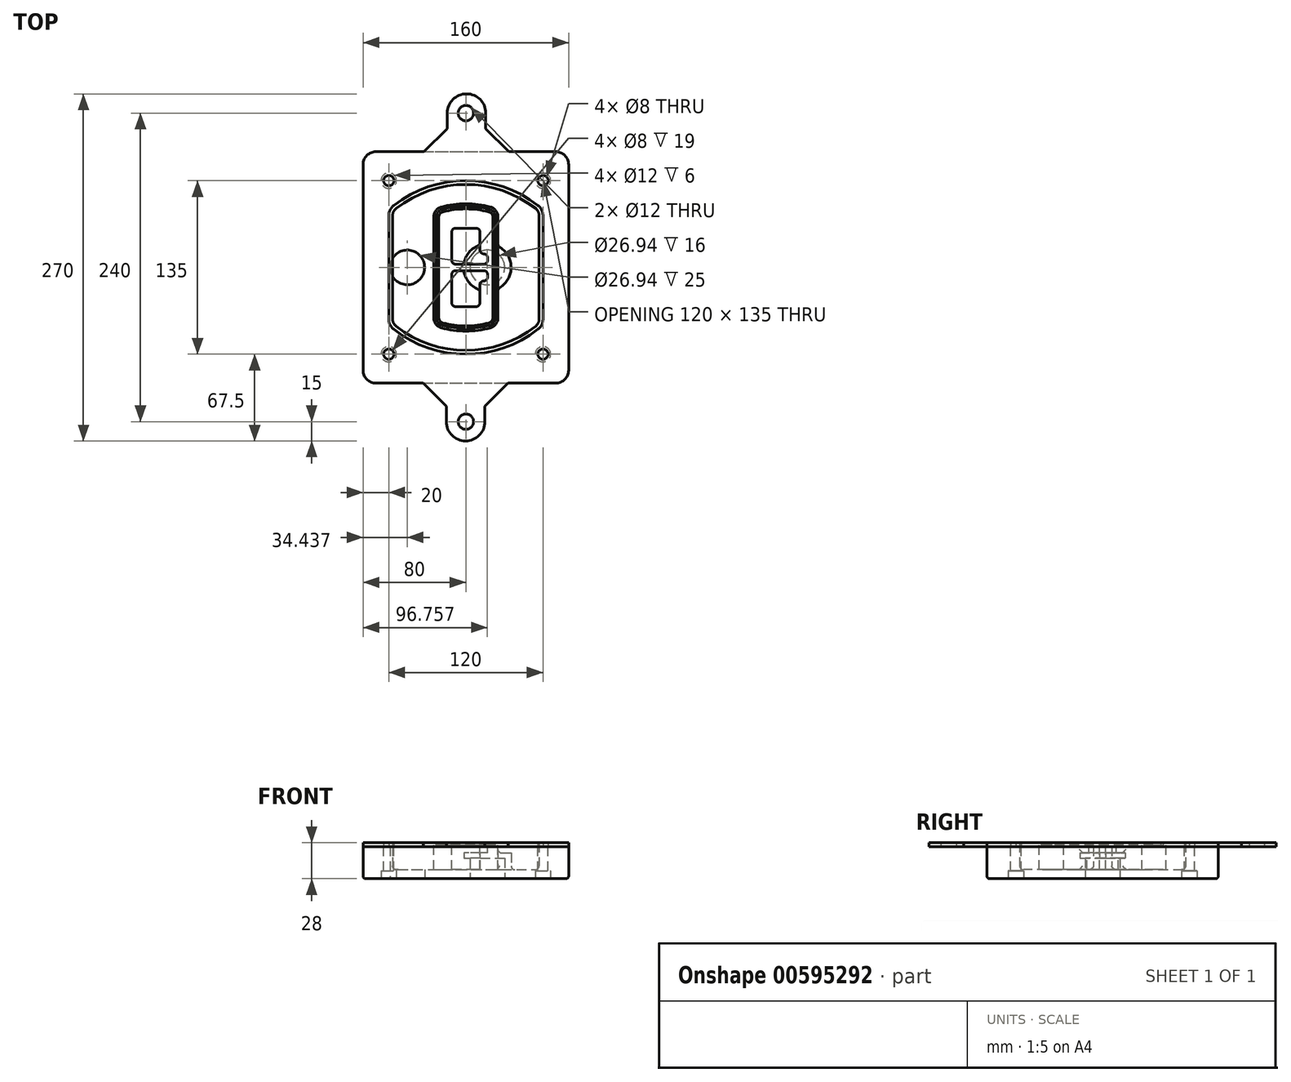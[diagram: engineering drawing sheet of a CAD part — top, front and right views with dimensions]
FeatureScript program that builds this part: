
annotation { "Feature Type Name" : "Feature", "Feature Type Description" : "" }
export const myFeature = defineFeature(function(context is Context, id is Id, definition is map)
    precondition{}
    {
        {
            var Q0;
            Q0=qCreatedBy(makeId("Top.planeOp"),FACE);
            var sketch = newSketch(context, id + "F0", { "sketchPlane" : qUnion([Q0])});
            skPoint(sketch, "E0.rect.middle", {"position": v(0, 0) * mm});
            skLineSegment(sketch, "E1.bottom", {"start": v(-70, -90) * mm, "end": v(70, -90) * mm});
            skLineSegment(sketch, "E1.top", {"start": v(-70, 90) * mm, "end": v(70, 90) * mm});
            skLineSegment(sketch, "E1.left", {"start": v(-80, -80) * mm, "end": v(-80, 80) * mm});
            skLineSegment(sketch, "E1.right", {"start": v(80, -80) * mm, "end": v(80, 80) * mm});
            skLineSegment(sketch, "E2", {"start": v(-80, 90) * mm, "end": v(80, -90) * mm, "construction": true});
            skLineSegment(sketch, "E3", {"start": v(80, 90) * mm, "end": v(-80, -90) * mm, "construction": true});
            skCircle(sketch, "E4", {"center": v(-60, 67.5) * mm, "radius": 4 * mm});
            skCircle(sketch, "E5", {"center": v(60, 67.5) * mm, "radius": 4 * mm});
            skCircle(sketch, "E6", {"center": v(60, -67.5) * mm, "radius": 4 * mm});
            skCircle(sketch, "E7", {"center": v(-60, -67.5) * mm, "radius": 4 * mm});
            skLineSegment(sketch, "E8", {"start": v(-60, 67.5) * mm, "end": v(60, 67.5) * mm, "construction": true});
            skLineSegment(sketch, "E9", {"start": v(60, 67.5) * mm, "end": v(60, -67.5) * mm, "construction": true});
            skLineSegment(sketch, "E10", {"start": v(60, -67.5) * mm, "end": v(-60, -67.5) * mm, "construction": true});
            skLineSegment(sketch, "E11", {"start": v(-60, -67.5) * mm, "end": v(-60, 67.5) * mm, "construction": true});
            skLineSegment(sketch, "E12", {"start": v(-60, 40.3) * mm, "end": v(-60, -40.3) * mm});
            skLineSegment(sketch, "E13", {"start": v(60, 40.3) * mm, "end": v(60, -40.3) * mm});
            skArc(sketch, "E14", {"start": v(56.15, 48.18) * mm, "mid": v(0, 67.5) * mm, "end": v(-56.15, 48.18) * mm});
            skArc(sketch, "E15", {"start": v(-56.15, -48.18) * mm, "mid": v(0, -67.5) * mm, "end": v(56.15, -48.18) * mm});
            skLineSegment(sketch, "E16", {"start": v(-60, 0) * mm, "end": v(60, 0) * mm, "construction": true});
            skPoint(sketch, "E17.visualSharp", {"position": v(-60, -45) * mm});
            skArc(sketch, "E17.filletArc", {"start": v(-60, -40.3) * mm, "mid": v(-58.99, -44.68) * mm, "end": v(-56.15, -48.18) * mm});
            skPoint(sketch, "E18.visualSharp", {"position": v(-60, 45) * mm});
            skArc(sketch, "E18.filletArc", {"start": v(-56.15, 48.18) * mm, "mid": v(-58.99, 44.68) * mm, "end": v(-60, 40.3) * mm});
            skPoint(sketch, "E19.visualSharp", {"position": v(60, 45) * mm});
            skArc(sketch, "E19.filletArc", {"start": v(60, 40.3) * mm, "mid": v(58.99, 44.68) * mm, "end": v(56.15, 48.18) * mm});
            skPoint(sketch, "E20.visualSharp", {"position": v(60, -45) * mm});
            skArc(sketch, "E20.filletArc", {"start": v(56.15, -48.18) * mm, "mid": v(58.99, -44.68) * mm, "end": v(60, -40.3) * mm});
            skPoint(sketch, "E21.visualSharp", {"position": v(-80, 90) * mm});
            skArc(sketch, "E21.filletArc", {"start": v(-70, 90) * mm, "mid": v(-77.07, 87.07) * mm, "end": v(-80, 80) * mm});
            skPoint(sketch, "E22.visualSharp", {"position": v(80, 90) * mm});
            skArc(sketch, "E22.filletArc", {"start": v(80, 80) * mm, "mid": v(77.07, 87.07) * mm, "end": v(70, 90) * mm});
            skPoint(sketch, "E23.visualSharp", {"position": v(80, -90) * mm});
            skArc(sketch, "E23.filletArc", {"start": v(70, -90) * mm, "mid": v(77.07, -87.07) * mm, "end": v(80, -80) * mm});
            skPoint(sketch, "E24.visualSharp", {"position": v(-80, -90) * mm});
            skArc(sketch, "E24.filletArc", {"start": v(-80, -80) * mm, "mid": v(-77.07, -87.07) * mm, "end": v(-70, -90) * mm});
            skArc(sketch, "E25.0", {"start": v(57, 40.3) * mm, "mid": v(56.3, 43.36) * mm, "end": v(54.3, 45.81) * mm});
            skLineSegment(sketch, "E25.1", {"start": v(57, 40.3) * mm, "end": v(57, -40.3) * mm});
            skArc(sketch, "E25.2", {"start": v(54.3, -45.81) * mm, "mid": v(56.3, -43.36) * mm, "end": v(57, -40.3) * mm});
            skArc(sketch, "E25.3", {"start": v(-54.3, -45.81) * mm, "mid": v(0, -64.5) * mm, "end": v(54.3, -45.81) * mm});
            skArc(sketch, "E25.4", {"start": v(-57, -40.3) * mm, "mid": v(-56.3, -43.36) * mm, "end": v(-54.3, -45.81) * mm});
            skArc(sketch, "E25.5", {"start": v(54.3, 45.81) * mm, "mid": v(0, 64.5) * mm, "end": v(-54.3, 45.81) * mm});
            skLineSegment(sketch, "E25.6", {"start": v(-57, 40.3) * mm, "end": v(-57, -40.3) * mm});
            skArc(sketch, "E25.7", {"start": v(-54.3, 45.81) * mm, "mid": v(-56.3, 43.36) * mm, "end": v(-57, 40.3) * mm});
            skArc(sketch, "E26.0", {"start": v(-58.62, 51.33) * mm, "mid": v(-62.58, 46.43) * mm, "end": v(-64, 40.3) * mm});
            skArc(sketch, "E26.1", {"start": v(58.62, 51.33) * mm, "mid": v(0, 71.5) * mm, "end": v(-58.62, 51.33) * mm});
            skArc(sketch, "E26.2", {"start": v(64, 40.3) * mm, "mid": v(62.58, 46.43) * mm, "end": v(58.62, 51.33) * mm});
            skLineSegment(sketch, "E26.3", {"start": v(64, 40.3) * mm, "end": v(64, -40.3) * mm});
            skArc(sketch, "E26.4", {"start": v(58.62, -51.33) * mm, "mid": v(62.58, -46.43) * mm, "end": v(64, -40.3) * mm});
            skLineSegment(sketch, "E26.5", {"start": v(-64, 40.3) * mm, "end": v(-64, -40.3) * mm});
            skArc(sketch, "E26.6", {"start": v(-58.62, -51.33) * mm, "mid": v(0, -71.5) * mm, "end": v(58.62, -51.33) * mm});
            skArc(sketch, "E26.7", {"start": v(-64, -40.3) * mm, "mid": v(-62.58, -46.43) * mm, "end": v(-58.62, -51.33) * mm});
            skSolve(sketch);
        }
        {
            var Q0;
            Q0=makeQuery(id+"F0.imprint","IMPRINT",FACE,{"disambiguationData":[TD([[makeQuery(id+"F0.imprint","IMPRINT",EDGE,{"derivedFrom":sQuery(id+"F0.wireOp",EDGE,"E1.bottom")}),1.0]])]});
            var Q1;
            Q1=makeQuery(id+"F0.imprint","IMPRINT",FACE,{"disambiguationData":[TD([[makeQuery(id+"F0.imprint","IMPRINT",EDGE,{"derivedFrom":sQuery(id+"F0.wireOp",EDGE,"E12")}),1.0]])]});
            var Q2;
            Q2=makeQuery(id+"F0.imprint","IMPRINT",FACE,{"disambiguationData":[TD([[makeQuery(id+"F0.imprint","IMPRINT",EDGE,{"derivedFrom":sQuery(id+"F0.wireOp",EDGE,"E25.0")}),1.0]])]});
            var Q3;
            Q3=makeQuery(id+"F0.imprint","IMPRINT",FACE,{"disambiguationData":[TD([[makeQuery(id+"F0.imprint","IMPRINT",EDGE,{"derivedFrom":sQuery(id+"F0.wireOp",EDGE,"E12")}),-1.0]])]});
            extrude(context, id + "F1", {"entities" : qUnion([Q0, Q1, Q2, Q3]), "oppositeDirection" : true, "depth" : 25 * mm});
        }
        {
            var Q0;
            Q0=makeQuery(id+"F0.imprint","IMPRINT",FACE,{"disambiguationData":[TD([[makeQuery(id+"F0.imprint","IMPRINT",EDGE,{"derivedFrom":sQuery(id+"F0.wireOp",EDGE,"E12")}),1.0]])]});
            extrude(context, id + "F2", {"entities" : qUnion([Q0]), "operationType" : NewBodyOperationType.ADD, "depth" : 3 * mm});
        }
        {
            var Q0;
            Q0=makeQuery(id+"F0.imprint","IMPRINT",FACE,{"disambiguationData":[TD([[makeQuery(id+"F0.imprint","IMPRINT",EDGE,{"derivedFrom":sQuery(id+"F0.wireOp",EDGE,"E25.0")}),1.0]])]});
            extrude(context, id + "F3", {"entities" : qUnion([Q0]), "operationType" : NewBodyOperationType.REMOVE, "oppositeDirection" : true, "depth" : 18 * mm});
        }
        {
            var Q0;
            Q0=makeQuery(id+"F2.opExtrude","CAP_FACE",FACE,{"disambiguationData":[OSD([sQuery(id+"F0.wireOp",EDGE,"E12"),sQuery(id+"F0.wireOp",EDGE,"E13"),sQuery(id+"F0.wireOp",EDGE,"E14"),sQuery(id+"F0.wireOp",EDGE,"E15"),sQuery(id+"F0.wireOp",EDGE,"E17.filletArc"),sQuery(id+"F0.wireOp",EDGE,"E18.filletArc"),sQuery(id+"F0.wireOp",EDGE,"E19.filletArc"),sQuery(id+"F0.wireOp",EDGE,"E20.filletArc"),sQuery(id+"F0.wireOp",EDGE,"E25.0"),sQuery(id+"F0.wireOp",EDGE,"E25.1"),sQuery(id+"F0.wireOp",EDGE,"E25.2"),sQuery(id+"F0.wireOp",EDGE,"E25.3"),sQuery(id+"F0.wireOp",EDGE,"E25.4"),sQuery(id+"F0.wireOp",EDGE,"E25.5"),sQuery(id+"F0.wireOp",EDGE,"E25.6"),sQuery(id+"F0.wireOp",EDGE,"E25.7")])],"isStart":false});
            var sketch = newSketch(context, id + "F4", { "sketchPlane" : qUnion([Q0])});
            skArc(sketch, "E27.0", {"start": v(-19.08, -46.97) * mm, "mid": v(0, -49.5) * mm, "end": v(19.08, -46.97) * mm});
            skArc(sketch, "E28.0", {"start": v(19.08, 46.97) * mm, "mid": v(0, 49.5) * mm, "end": v(-19.08, 46.97) * mm});
            skLineSegment(sketch, "E29", {"start": v(-25, 39.25) * mm, "end": v(-25, -39.25) * mm});
            skLineSegment(sketch, "E30", {"start": v(25, 39.25) * mm, "end": v(25, -39.25) * mm});
            skLineSegment(sketch, "E31", {"start": v(-25, 45.1) * mm, "end": v(25, 45.1) * mm, "construction": true});
            skLineSegment(sketch, "E32", {"start": v(-25, -45.1) * mm, "end": v(25, -45.1) * mm, "construction": true});
            skPoint(sketch, "E33.visualSharp", {"position": v(-25, 45.1) * mm});
            skArc(sketch, "E33.filletArc", {"start": v(-19.08, 46.97) * mm, "mid": v(-23.35, 44.11) * mm, "end": v(-25, 39.25) * mm});
            skPoint(sketch, "E34.visualSharp", {"position": v(25, 45.1) * mm});
            skArc(sketch, "E34.filletArc", {"start": v(25, 39.25) * mm, "mid": v(23.35, 44.11) * mm, "end": v(19.08, 46.97) * mm});
            skPoint(sketch, "E35.visualSharp", {"position": v(25, -45.1) * mm});
            skArc(sketch, "E35.filletArc", {"start": v(19.08, -46.97) * mm, "mid": v(23.35, -44.11) * mm, "end": v(25, -39.25) * mm});
            skPoint(sketch, "E36.visualSharp", {"position": v(-25, -45.1) * mm});
            skArc(sketch, "E36.filletArc", {"start": v(-25, -39.25) * mm, "mid": v(-23.35, -44.11) * mm, "end": v(-19.08, -46.97) * mm});
            skArc(sketch, "E37.0", {"start": v(54.3, 45.81) * mm, "mid": v(0, 64.5) * mm, "end": v(-54.3, 45.81) * mm});
            skArc(sketch, "E37.1", {"start": v(-54.3, 45.81) * mm, "mid": v(-56.3, 43.36) * mm, "end": v(-57, 40.3) * mm});
            skLineSegment(sketch, "E37.2", {"start": v(-57, 40.3) * mm, "end": v(-57, -40.3) * mm});
            skArc(sketch, "E37.3", {"start": v(-57, -40.3) * mm, "mid": v(-56.3, -43.36) * mm, "end": v(-54.3, -45.81) * mm});
            skArc(sketch, "E37.4", {"start": v(-54.3, -45.81) * mm, "mid": v(0, -64.5) * mm, "end": v(54.3, -45.81) * mm});
            skArc(sketch, "E37.5", {"start": v(54.3, -45.81) * mm, "mid": v(56.3, -43.36) * mm, "end": v(57, -40.3) * mm});
            skLineSegment(sketch, "E37.6", {"start": v(57, 40.3) * mm, "end": v(57, -40.3) * mm});
            skArc(sketch, "E37.7", {"start": v(57, 40.3) * mm, "mid": v(56.3, 43.36) * mm, "end": v(54.3, 45.81) * mm});
            skLineSegment(sketch, "E38.0", {"start": v(23, 39.25) * mm, "end": v(23, -39.25) * mm});
            skArc(sketch, "E38.1", {"start": v(18.56, -45.04) * mm, "mid": v(21.76, -42.9) * mm, "end": v(23, -39.25) * mm});
            skArc(sketch, "E38.2", {"start": v(-18.56, -45.04) * mm, "mid": v(0, -47.5) * mm, "end": v(18.56, -45.04) * mm});
            skArc(sketch, "E38.3", {"start": v(-23, -39.25) * mm, "mid": v(-21.76, -42.9) * mm, "end": v(-18.56, -45.04) * mm});
            skLineSegment(sketch, "E38.4", {"start": v(-23, 39.25) * mm, "end": v(-23, -39.25) * mm});
            skArc(sketch, "E38.5", {"start": v(23, 39.25) * mm, "mid": v(21.76, 42.9) * mm, "end": v(18.56, 45.04) * mm});
            skArc(sketch, "E38.6", {"start": v(-18.56, 45.04) * mm, "mid": v(-21.76, 42.9) * mm, "end": v(-23, 39.25) * mm});
            skArc(sketch, "E38.7", {"start": v(18.56, 45.04) * mm, "mid": v(0, 47.5) * mm, "end": v(-18.56, 45.04) * mm});
            skArc(sketch, "E39.0", {"start": v(21, 39.25) * mm, "mid": v(20.18, 41.68) * mm, "end": v(18.04, 43.1) * mm});
            skLineSegment(sketch, "E39.1", {"start": v(21, 39.25) * mm, "end": v(21, -39.25) * mm});
            skArc(sketch, "E39.2", {"start": v(18.04, -43.1) * mm, "mid": v(20.18, -41.68) * mm, "end": v(21, -39.25) * mm});
            skArc(sketch, "E39.3", {"start": v(-18.04, -43.1) * mm, "mid": v(0, -45.5) * mm, "end": v(18.04, -43.1) * mm});
            skArc(sketch, "E39.4", {"start": v(-21, -39.25) * mm, "mid": v(-20.18, -41.68) * mm, "end": v(-18.04, -43.1) * mm});
            skArc(sketch, "E39.5", {"start": v(18.04, 43.1) * mm, "mid": v(0, 45.5) * mm, "end": v(-18.04, 43.1) * mm});
            skLineSegment(sketch, "E39.6", {"start": v(-21, 39.25) * mm, "end": v(-21, -39.25) * mm});
            skArc(sketch, "E39.7", {"start": v(-18.04, 43.1) * mm, "mid": v(-20.18, 41.68) * mm, "end": v(-21, 39.25) * mm});
            skLineSegment(sketch, "E40", {"start": v(-25, 0) * mm, "end": v(25, 0) * mm, "construction": true});
            skLineSegment(sketch, "E41", {"start": v(-11, 5.5) * mm, "end": v(-11, 27.5) * mm});
            skLineSegment(sketch, "E42", {"start": v(-8, 30.5) * mm, "end": v(8, 30.5) * mm});
            skLineSegment(sketch, "E43", {"start": v(11, 27.5) * mm, "end": v(11, 13.5) * mm});
            skLineSegment(sketch, "E44", {"start": v(14, 10.5) * mm, "end": v(14, 10.5) * mm});
            skLineSegment(sketch, "E45", {"start": v(17, 7.5) * mm, "end": v(17, 5.5) * mm});
            skLineSegment(sketch, "E46", {"start": v(14, 2.5) * mm, "end": v(-8, 2.5) * mm});
            skPoint(sketch, "E47.visualSharp", {"position": v(-11, 30.5) * mm});
            skArc(sketch, "E47.filletArc", {"start": v(-8, 30.5) * mm, "mid": v(-10.12, 29.62) * mm, "end": v(-11, 27.5) * mm});
            skPoint(sketch, "E48.visualSharp", {"position": v(11, 30.5) * mm});
            skArc(sketch, "E48.filletArc", {"start": v(11, 27.5) * mm, "mid": v(10.12, 29.62) * mm, "end": v(8, 30.5) * mm});
            skPoint(sketch, "E49.visualSharp", {"position": v(11, 10.5) * mm});
            skArc(sketch, "E49.filletArc", {"start": v(11, 13.5) * mm, "mid": v(11.88, 11.38) * mm, "end": v(14, 10.5) * mm});
            skPoint(sketch, "E50.visualSharp", {"position": v(17, 10.5) * mm});
            skArc(sketch, "E50.filletArc", {"start": v(17, 7.5) * mm, "mid": v(16.12, 9.62) * mm, "end": v(14, 10.5) * mm});
            skPoint(sketch, "E51.visualSharp", {"position": v(17, 2.5) * mm});
            skArc(sketch, "E51.filletArc", {"start": v(14, 2.5) * mm, "mid": v(16.12, 3.38) * mm, "end": v(17, 5.5) * mm});
            skPoint(sketch, "E52.visualSharp", {"position": v(-11, 2.5) * mm});
            skArc(sketch, "E52.filletArc", {"start": v(-11, 5.5) * mm, "mid": v(-10.12, 3.38) * mm, "end": v(-8, 2.5) * mm});
            skLineSegment(sketch, "E53.0.MirrorCS", {"start": v(14, -2.5) * mm, "end": v(-8, -2.5) * mm});
            skArc(sketch, "E54.0.MirrorCS", {"start": v(-11, -5.5) * mm, "mid": v(-10.12, -3.38) * mm, "end": v(-8, -2.5) * mm});
            skLineSegment(sketch, "E55.0.MirrorCS", {"start": v(-11, -5.5) * mm, "end": v(-11, -27.5) * mm});
            skArc(sketch, "E56.0.MirrorCS", {"start": v(-8, -30.5) * mm, "mid": v(-10.12, -29.62) * mm, "end": v(-11, -27.5) * mm});
            skLineSegment(sketch, "E57.0.MirrorCS", {"start": v(-8, -30.5) * mm, "end": v(8, -30.5) * mm});
            skArc(sketch, "E58.0.MirrorCS", {"start": v(11, -27.5) * mm, "mid": v(10.12, -29.62) * mm, "end": v(8, -30.5) * mm});
            skLineSegment(sketch, "E59.0.MirrorCS", {"start": v(11, -27.5) * mm, "end": v(11, -13.5) * mm});
            skArc(sketch, "E60.0.MirrorCS", {"start": v(11, -13.5) * mm, "mid": v(11.88, -11.38) * mm, "end": v(14, -10.5) * mm});
            skArc(sketch, "E61.0.MirrorCS", {"start": v(17, -7.5) * mm, "mid": v(16.12, -9.62) * mm, "end": v(14, -10.5) * mm});
            skLineSegment(sketch, "E62.0.MirrorCS", {"start": v(17, -7.5) * mm, "end": v(17, -5.5) * mm});
            skArc(sketch, "E63.0.MirrorCS", {"start": v(14, -2.5) * mm, "mid": v(16.12, -3.38) * mm, "end": v(17, -5.5) * mm});
            skSolve(sketch);
        }
        {
            var Q0;
            Q0=makeQuery(id+"F4.imprint","IMPRINT",FACE,{"disambiguationData":[TD([[makeQuery(id+"F4.imprint","IMPRINT",EDGE,{"derivedFrom":sQuery(id+"F4.wireOp",EDGE,"E27.0")}),1.0]])]});
            var Q1;
            Q1=makeQuery(id+"F4.imprint","IMPRINT",FACE,{"disambiguationData":[TD([[makeQuery(id+"F4.imprint","IMPRINT",EDGE,{"derivedFrom":sQuery(id+"F4.wireOp",EDGE,"E38.0")}),-1.0]])]});
            var Q2;
            Q2=makeQuery(id+"F4.imprint","IMPRINT",FACE,{"disambiguationData":[TD([[makeQuery(id+"F4.imprint","IMPRINT",EDGE,{"derivedFrom":sQuery(id+"F4.wireOp",EDGE,"E39.0")}),1.0]])]});
            extrude(context, id + "F5", {"entities" : qUnion([Q0, Q1, Q2]), "operationType" : NewBodyOperationType.ADD, "endBound" : BoundingType.UP_TO_NEXT, "oppositeDirection" : true, "depth" : 25 * mm});
        }
        {
            var Q0;
            Q0=makeQuery(id+"F4.imprint","IMPRINT",FACE,{"disambiguationData":[TD([[makeQuery(id+"F4.imprint","IMPRINT",EDGE,{"derivedFrom":sQuery(id+"F4.wireOp",EDGE,"E38.0")}),-1.0]])]});
            extrude(context, id + "F6", {"entities" : qUnion([Q0]), "operationType" : NewBodyOperationType.REMOVE, "oppositeDirection" : true, "depth" : 2 * mm});
        }
        {
            var Q0;
            Q0=makeQuery(id+"F1.opExtrude","CAP_FACE",FACE,{"disambiguationData":[OSD([sQuery(id+"F0.wireOp",EDGE,"E1.bottom"),sQuery(id+"F0.wireOp",EDGE,"E1.top"),sQuery(id+"F0.wireOp",EDGE,"E1.left"),sQuery(id+"F0.wireOp",EDGE,"E1.right"),sQuery(id+"F0.wireOp",EDGE,"E4"),sQuery(id+"F0.wireOp",EDGE,"E5"),sQuery(id+"F0.wireOp",EDGE,"E6"),sQuery(id+"F0.wireOp",EDGE,"E7"),sQuery(id+"F0.wireOp",EDGE,"E21.filletArc"),sQuery(id+"F0.wireOp",EDGE,"E22.filletArc"),sQuery(id+"F0.wireOp",EDGE,"E23.filletArc"),sQuery(id+"F0.wireOp",EDGE,"E24.filletArc")])],"isStart":false});
            var sketch = newSketch(context, id + "F7", { "sketchPlane" : qUnion([Q0])});
            skCircle(sketch, "E64", {"center": v(16.76, 0) * mm, "radius": 13.47 * mm});
            skCircle(sketch, "E65", {"center": v(-45.56, 0) * mm, "radius": 13.47 * mm});
            skLineSegment(sketch, "E66", {"start": v(80, 0) * mm, "end": v(-80, 0) * mm});
            skCircle(sketch, "E67", {"center": v(16.76, 0) * mm, "radius": 18.47 * mm});
            skCircle(sketch, "E68", {"center": v(60, -67.5) * mm, "radius": 6 * mm});
            skCircle(sketch, "E69", {"center": v(-60, -67.5) * mm, "radius": 6 * mm});
            skCircle(sketch, "E70", {"center": v(-60, 67.5) * mm, "radius": 6 * mm});
            skCircle(sketch, "E71", {"center": v(60, 67.5) * mm, "radius": 6 * mm});
            skSolve(sketch);
        }
        {
            var Q0;
            {var subQ1=sQuery(id+"F7.wireOp",EDGE,"E66");var subQ4=sQuery(id+"F7.wireOp",EDGE,"E64");var subQ6=makeQuery(id+"F7.imprint","INTERSECT",VERTEX,{"disambiguationData":[OD(0.0)],"derivedFrom":[subQ4,subQ1]});Q0=makeQuery(id+"F7.imprint","IMPRINT",FACE,{"disambiguationData":[TD([[makeQuery(id+"F7.imprint","IMPRINT",EDGE,{"disambiguationData":[TD([[subQ6,-1.0]])],"derivedFrom":subQ4}),-1.0]])]});}
            var Q1;
            {var subQ0=sQuery(id+"F7.wireOp",EDGE,"E66");var subQ1=sQuery(id+"F7.wireOp",EDGE,"E64");var subQ3=makeQuery(id+"F7.imprint","INTERSECT",VERTEX,{"disambiguationData":[OD(0.0)],"derivedFrom":[subQ1,subQ0]});Q1=makeQuery(id+"F7.imprint","IMPRINT",FACE,{"disambiguationData":[TD([[makeQuery(id+"F7.imprint","IMPRINT",EDGE,{"disambiguationData":[TD([[subQ3,-1.0]])],"derivedFrom":subQ1}),1.0]])]});}
            var Q2;
            {var subQ0=sQuery(id+"F7.wireOp",EDGE,"E66");var subQ1=sQuery(id+"F7.wireOp",EDGE,"E64");var subQ3=makeQuery(id+"F7.imprint","INTERSECT",VERTEX,{"disambiguationData":[OD(0.0)],"derivedFrom":[subQ1,subQ0]});Q2=makeQuery(id+"F7.imprint","IMPRINT",FACE,{"disambiguationData":[TD([[makeQuery(id+"F7.imprint","IMPRINT",EDGE,{"disambiguationData":[TD([[subQ3,1.0]])],"derivedFrom":subQ1}),1.0]])]});}
            var Q3;
            {var subQ1=sQuery(id+"F7.wireOp",EDGE,"E66");var subQ4=sQuery(id+"F7.wireOp",EDGE,"E64");var subQ6=makeQuery(id+"F7.imprint","INTERSECT",VERTEX,{"disambiguationData":[OD(0.0)],"derivedFrom":[subQ4,subQ1]});Q3=makeQuery(id+"F7.imprint","IMPRINT",FACE,{"disambiguationData":[TD([[makeQuery(id+"F7.imprint","IMPRINT",EDGE,{"disambiguationData":[TD([[subQ6,1.0]])],"derivedFrom":subQ4}),-1.0]])]});}
            extrude(context, id + "F8", {"entities" : qUnion([Q0, Q1, Q2, Q3]), "operationType" : NewBodyOperationType.ADD, "oppositeDirection" : true, "depth" : 20 * mm});
        }
        {
            var Q0;
            {var subQ0=sQuery(id+"F7.wireOp",EDGE,"E66");var subQ1=sQuery(id+"F7.wireOp",EDGE,"E64");var subQ3=makeQuery(id+"F7.imprint","INTERSECT",VERTEX,{"disambiguationData":[OD(0.0)],"derivedFrom":[subQ1,subQ0]});Q0=makeQuery(id+"F7.imprint","IMPRINT",FACE,{"disambiguationData":[TD([[makeQuery(id+"F7.imprint","IMPRINT",EDGE,{"disambiguationData":[TD([[subQ3,-1.0]])],"derivedFrom":subQ1}),1.0]])]});}
            var Q1;
            {var subQ0=sQuery(id+"F7.wireOp",EDGE,"E66");var subQ1=sQuery(id+"F7.wireOp",EDGE,"E64");var subQ3=makeQuery(id+"F7.imprint","INTERSECT",VERTEX,{"disambiguationData":[OD(0.0)],"derivedFrom":[subQ1,subQ0]});Q1=makeQuery(id+"F7.imprint","IMPRINT",FACE,{"disambiguationData":[TD([[makeQuery(id+"F7.imprint","IMPRINT",EDGE,{"disambiguationData":[TD([[subQ3,1.0]])],"derivedFrom":subQ1}),1.0]])]});}
            extrude(context, id + "F9", {"entities" : qUnion([Q0, Q1]), "operationType" : NewBodyOperationType.REMOVE, "oppositeDirection" : true, "depth" : 16 * mm});
        }
        {
            var Q0;
            {var subQ0=sQuery(id+"F7.wireOp",EDGE,"E66");var subQ1=sQuery(id+"F7.wireOp",EDGE,"E65");var subQ3=makeQuery(id+"F7.imprint","INTERSECT",VERTEX,{"disambiguationData":[OD(0.0)],"derivedFrom":[subQ1,subQ0]});Q0=makeQuery(id+"F7.imprint","IMPRINT",FACE,{"disambiguationData":[TD([[makeQuery(id+"F7.imprint","IMPRINT",EDGE,{"disambiguationData":[TD([[subQ3,-1.0]])],"derivedFrom":subQ1}),1.0]])]});}
            var Q1;
            {var subQ0=sQuery(id+"F7.wireOp",EDGE,"E66");var subQ1=sQuery(id+"F7.wireOp",EDGE,"E65");var subQ3=makeQuery(id+"F7.imprint","INTERSECT",VERTEX,{"disambiguationData":[OD(0.0)],"derivedFrom":[subQ1,subQ0]});Q1=makeQuery(id+"F7.imprint","IMPRINT",FACE,{"disambiguationData":[TD([[makeQuery(id+"F7.imprint","IMPRINT",EDGE,{"disambiguationData":[TD([[subQ3,1.0]])],"derivedFrom":subQ1}),1.0]])]});}
            extrude(context, id + "F10", {"entities" : qUnion([Q0, Q1]), "operationType" : NewBodyOperationType.REMOVE, "oppositeDirection" : true, "depth" : 25 * mm});
        }
        {
            var Q0;
            Q0=makeQuery(id+"F7.imprint","IMPRINT",FACE,{"disambiguationData":[TD([[makeQuery(id+"F7.imprint","IMPRINT",EDGE,{"derivedFrom":sQuery(id+"F7.wireOp",EDGE,"E68")}),1.0]])]});
            var Q1;
            Q1=makeQuery(id+"F7.imprint","IMPRINT",FACE,{"disambiguationData":[TD([[makeQuery(id+"F7.imprint","IMPRINT",EDGE,{"derivedFrom":makeQuery(id+"F1.opExtrude","CAP_EDGE",EDGE,{"disambiguationData":[OSD([sQuery(id+"F0.wireOp",EDGE,"E5")])],"isStart":false})}),-1.0]])]});
            var Q2;
            Q2=makeQuery(id+"F7.imprint","IMPRINT",FACE,{"disambiguationData":[TD([[makeQuery(id+"F7.imprint","IMPRINT",EDGE,{"derivedFrom":sQuery(id+"F7.wireOp",EDGE,"E69")}),1.0]])]});
            var Q3;
            Q3=makeQuery(id+"F7.imprint","IMPRINT",FACE,{"disambiguationData":[TD([[makeQuery(id+"F7.imprint","IMPRINT",EDGE,{"derivedFrom":makeQuery(id+"F1.opExtrude","CAP_EDGE",EDGE,{"disambiguationData":[OSD([sQuery(id+"F0.wireOp",EDGE,"E4")])],"isStart":false})}),-1.0]])]});
            var Q4;
            Q4=makeQuery(id+"F7.imprint","IMPRINT",FACE,{"disambiguationData":[TD([[makeQuery(id+"F7.imprint","IMPRINT",EDGE,{"derivedFrom":sQuery(id+"F7.wireOp",EDGE,"E70")}),1.0]])]});
            var Q5;
            Q5=makeQuery(id+"F7.imprint","IMPRINT",FACE,{"disambiguationData":[TD([[makeQuery(id+"F7.imprint","IMPRINT",EDGE,{"derivedFrom":makeQuery(id+"F1.opExtrude","CAP_EDGE",EDGE,{"disambiguationData":[OSD([sQuery(id+"F0.wireOp",EDGE,"E7")])],"isStart":false})}),-1.0]])]});
            var Q6;
            Q6=makeQuery(id+"F7.imprint","IMPRINT",FACE,{"disambiguationData":[TD([[makeQuery(id+"F7.imprint","IMPRINT",EDGE,{"derivedFrom":sQuery(id+"F7.wireOp",EDGE,"E71")}),1.0]])]});
            var Q7;
            Q7=makeQuery(id+"F7.imprint","IMPRINT",FACE,{"disambiguationData":[TD([[makeQuery(id+"F7.imprint","IMPRINT",EDGE,{"derivedFrom":makeQuery(id+"F1.opExtrude","CAP_EDGE",EDGE,{"disambiguationData":[OSD([sQuery(id+"F0.wireOp",EDGE,"E6")])],"isStart":false})}),-1.0]])]});
            extrude(context, id + "F11", {"entities" : qUnion([Q0, Q1, Q2, Q3, Q4, Q5, Q6, Q7]), "operationType" : NewBodyOperationType.REMOVE, "oppositeDirection" : true, "depth" : 6 * mm});
        }
        {
            var Q0;
            Q0=makeQuery(id+"F9.boolean.opBoolean","COPY",FACE,{"derivedFrom":makeQuery(id+"F9.opExtrude","CAP_FACE",FACE,{"disambiguationData":[OSD([sQuery(id+"F7.wireOp",EDGE,"E64")])],"isStart":false})});
            var sketch = newSketch(context, id + "F12", { "sketchPlane" : qUnion([Q0])});
            skArc(sketch, "E72.0", {"start": v(11, 17.55) * mm, "mid": v(2.57, 11.82) * mm, "end": v(-1.54, 2.5) * mm});
            skArc(sketch, "E72.1", {"start": v(-1.54, -2.5) * mm, "mid": v(2.57, -11.82) * mm, "end": v(11, -17.55) * mm});
            skLineSegment(sketch, "E73", {"start": v(-1.54, -2.5) * mm, "end": v(14, -2.5) * mm});
            skLineSegment(sketch, "E74.0", {"start": v(14, 2.5) * mm, "end": v(-1.54, 2.5) * mm});
            skArc(sketch, "E74.1", {"start": v(14, 2.5) * mm, "mid": v(16.12, 3.38) * mm, "end": v(17, 5.5) * mm});
            skLineSegment(sketch, "E74.2", {"start": v(17, 7.5) * mm, "end": v(17, 5.5) * mm});
            skArc(sketch, "E74.3", {"start": v(17, 7.5) * mm, "mid": v(16.12, 9.62) * mm, "end": v(14, 10.5) * mm});
            skArc(sketch, "E74.4", {"start": v(11, 13.5) * mm, "mid": v(11.88, 11.38) * mm, "end": v(14, 10.5) * mm});
            skLineSegment(sketch, "E74.5", {"start": v(11, 17.55) * mm, "end": v(11, 13.5) * mm});
            skLineSegment(sketch, "E74.7", {"start": v(14, -2.5) * mm, "end": v(-1.54, -2.5) * mm});
            skArc(sketch, "E74.8", {"start": v(14, -2.5) * mm, "mid": v(16.12, -3.38) * mm, "end": v(17, -5.5) * mm});
            skLineSegment(sketch, "E74.9", {"start": v(17, -7.5) * mm, "end": v(17, -5.5) * mm});
            skArc(sketch, "E74.10", {"start": v(17, -7.5) * mm, "mid": v(16.12, -9.62) * mm, "end": v(14, -10.5) * mm});
            skArc(sketch, "E74.11", {"start": v(11, -13.5) * mm, "mid": v(11.88, -11.38) * mm, "end": v(14, -10.5) * mm});
            skLineSegment(sketch, "E74.12", {"start": v(11, -17.55) * mm, "end": v(11, -13.5) * mm});
            skPoint(sketch, "E75.orphan", {"position": v(11, -27.5) * mm});
            skPoint(sketch, "E76.orphan", {"position": v(-8, -2.5) * mm});
            skPoint(sketch, "E77.orphan", {"position": v(-8, 2.5) * mm});
            skPoint(sketch, "E78.orphan", {"position": v(11, 27.5) * mm});
            skSolve(sketch);
        }
        {
            var Q0;
            {var subQ7=sQuery(id+"F12.wireOp",EDGE,"E72.0");var subQ14=sQuery(id+"F12.wireOp",EDGE,"E72.1");var subQ16=sQuery(id+"F12.wireOp",EDGE,"E74.1");var subQ18=sQuery(id+"F12.wireOp",EDGE,"E74.8");Q0=qUnion([makeQuery(id+"F12.imprint","IMPRINT",FACE,{"disambiguationData":[TD([[makeQuery(id+"F12.imprint","IMPRINT",EDGE,{"derivedFrom":subQ7}),1.0]])]}),makeQuery(id+"F12.imprint","IMPRINT",FACE,{"disambiguationData":[TD([[makeQuery(id+"F12.imprint","IMPRINT",EDGE,{"derivedFrom":subQ14}),1.0]])]}),makeQuery(id+"F12.imprint","IMPRINT",FACE,{"disambiguationData":[TD([[makeQuery(id+"F12.imprint","IMPRINT",EDGE,{"derivedFrom":subQ16}),1.0]])]}),makeQuery(id+"F12.imprint","IMPRINT",FACE,{"disambiguationData":[TD([[makeQuery(id+"F12.imprint","IMPRINT",EDGE,{"derivedFrom":subQ18}),-1.0]])]})]);}
            var Q1;
            Q1=makeQuery(id+"F5.boolean.opBoolean","SPLIT",FACE,{"disambiguationData":[TD([makeQuery(id+"F5.opExtrude","SWEPT_FACE",FACE,{"disambiguationData":[OSD([sQuery(id+"F4.wireOp",EDGE,"E41")])]})])],"derivedFrom":makeQuery(id+"F3.boolean.opBoolean","COPY",FACE,{"derivedFrom":makeQuery(id+"F3.opExtrude","CAP_FACE",FACE,{"disambiguationData":[OSD([sQuery(id+"F0.wireOp",EDGE,"E25.0"),sQuery(id+"F0.wireOp",EDGE,"E25.1"),sQuery(id+"F0.wireOp",EDGE,"E25.2"),sQuery(id+"F0.wireOp",EDGE,"E25.3"),sQuery(id+"F0.wireOp",EDGE,"E25.4"),sQuery(id+"F0.wireOp",EDGE,"E25.5"),sQuery(id+"F0.wireOp",EDGE,"E25.6"),sQuery(id+"F0.wireOp",EDGE,"E25.7")])],"isStart":false})})});
            extrude(context, id + "F13", {"entities" : qUnion([Q0]), "operationType" : NewBodyOperationType.REMOVE, "endBound" : BoundingType.UP_TO_SURFACE, "endBoundEntityFace" : qUnion([Q1]), "depth" : 25 * mm});
        }
        {
            var Q0;
            Q0=makeQuery(id+"F3.boolean.opBoolean","COPY",EDGE,{"derivedFrom":makeQuery(id+"F3.opExtrude","CAP_EDGE",EDGE,{"disambiguationData":[OSD([sQuery(id+"F0.wireOp",EDGE,"E25.6")])],"isStart":false})});
            var Q1;
            Q1=makeQuery(id+"F8.boolean.opBoolean","INTERSECT",EDGE,{"derivedFrom":[makeQuery(id+"F5.opExtrude","SWEPT_FACE",FACE,{"disambiguationData":[OSD([sQuery(id+"F4.wireOp",EDGE,"E30")])]}),makeQuery(id+"F8.opExtrude","CAP_FACE",FACE,{"disambiguationData":[OSD([sQuery(id+"F7.wireOp",EDGE,"E67")])],"isStart":false})]});
            var Q2;
            Q2=makeQuery(id+"F8.boolean.opBoolean","INTERSECT",EDGE,{"disambiguationData":[OD(1.0)],"derivedFrom":[makeQuery(id+"F5.opExtrude","SWEPT_FACE",FACE,{"disambiguationData":[OSD([sQuery(id+"F4.wireOp",EDGE,"E30")])]}),makeQuery(id+"F8.opExtrude","SWEPT_FACE",FACE,{"disambiguationData":[OSD([sQuery(id+"F7.wireOp",EDGE,"E67")])]})]});
            var Q3;
            {var subQ0=makeQuery(id+"F3.boolean.opBoolean","COPY",FACE,{"derivedFrom":makeQuery(id+"F3.opExtrude","CAP_FACE",FACE,{"disambiguationData":[OSD([sQuery(id+"F0.wireOp",EDGE,"E25.0"),sQuery(id+"F0.wireOp",EDGE,"E25.1"),sQuery(id+"F0.wireOp",EDGE,"E25.2"),sQuery(id+"F0.wireOp",EDGE,"E25.3"),sQuery(id+"F0.wireOp",EDGE,"E25.4"),sQuery(id+"F0.wireOp",EDGE,"E25.5"),sQuery(id+"F0.wireOp",EDGE,"E25.6"),sQuery(id+"F0.wireOp",EDGE,"E25.7")])],"isStart":false})});var subQ1=sQuery(id+"F4.wireOp",EDGE,"E30");Q3=makeQuery(id+"F8.boolean.opBoolean","SPLIT",EDGE,{"disambiguationData":[TD([makeQuery(id+"F5.opExtrude","SWEPT_FACE",FACE,{"disambiguationData":[OSD([sQuery(id+"F4.wireOp",EDGE,"E35.filletArc")])]})])],"derivedFrom":makeQuery(id+"F5.opExtrude","TWEAK_EDGE",EDGE,{"derivedFrom":[subQ0,makeQuery(id+"F4.imprint","IMPRINT",EDGE,{"derivedFrom":subQ1})]})});}
            var Q4;
            {var subQ0=sQuery(id+"F0.wireOp",EDGE,"E25.0");var subQ1=sQuery(id+"F0.wireOp",EDGE,"E25.1");var subQ2=sQuery(id+"F0.wireOp",EDGE,"E25.2");var subQ3=sQuery(id+"F0.wireOp",EDGE,"E25.3");var subQ4=sQuery(id+"F0.wireOp",EDGE,"E25.4");var subQ5=sQuery(id+"F0.wireOp",EDGE,"E25.5");var subQ6=sQuery(id+"F0.wireOp",EDGE,"E25.6");var subQ7=sQuery(id+"F0.wireOp",EDGE,"E25.7");Q4=makeQuery(id+"F8.boolean.opBoolean","INTERSECT",EDGE,{"derivedFrom":[makeQuery(id+"F5.boolean.opBoolean","SPLIT",FACE,{"disambiguationData":[TD([makeQuery(id+"F2.opExtrude","SWEPT_FACE",FACE,{"disambiguationData":[OSD([subQ0])]})])],"derivedFrom":makeQuery(id+"F3.boolean.opBoolean","COPY",FACE,{"derivedFrom":makeQuery(id+"F3.opExtrude","CAP_FACE",FACE,{"disambiguationData":[OSD([subQ0,subQ1,subQ2,subQ3,subQ4,subQ5,subQ6,subQ7])],"isStart":false})})}),makeQuery(id+"F8.opExtrude","SWEPT_FACE",FACE,{"disambiguationData":[OSD([sQuery(id+"F7.wireOp",EDGE,"E67")])]})]});}
            var Q5;
            Q5=makeQuery(id+"F8.boolean.opBoolean","INTERSECT",EDGE,{"disambiguationData":[OD(0.0)],"derivedFrom":[makeQuery(id+"F5.opExtrude","SWEPT_FACE",FACE,{"disambiguationData":[OSD([sQuery(id+"F4.wireOp",EDGE,"E30")])]}),makeQuery(id+"F8.opExtrude","SWEPT_FACE",FACE,{"disambiguationData":[OSD([sQuery(id+"F7.wireOp",EDGE,"E67")])]})]});
            fillet(context, id + "F14", {"entities" : qUnion([Q0, Q1, Q2, Q3, Q4, Q5]), "radius" : 3 * mm, "tangentPropagation" : true, "allowEdgeOverflow" : false});
        }
        {
            var Q0;
            Q0=makeQuery(id+"F1.opExtrude","CAP_EDGE",EDGE,{"disambiguationData":[OSD([sQuery(id+"F0.wireOp",EDGE,"E1.bottom")])],"isStart":false});
            fillet(context, id + "F15", {"entities" : qUnion([Q0]), "radius" : 2 * mm, "tangentPropagation" : true, "allowEdgeOverflow" : false});
        }
        {
            var Q0;
            {var subQ0=sQuery(id+"F0.wireOp",EDGE,"E21.filletArc");var subQ1=sQuery(id+"F0.wireOp",EDGE,"E7");var subQ2=sQuery(id+"F0.wireOp",EDGE,"E6");var subQ3=sQuery(id+"F0.wireOp",EDGE,"E5");var subQ4=sQuery(id+"F0.wireOp",EDGE,"E4");var subQ5=sQuery(id+"F0.wireOp",EDGE,"E22.filletArc");var subQ6=sQuery(id+"F0.wireOp",EDGE,"E1.bottom");var subQ7=sQuery(id+"F0.wireOp",EDGE,"E1.right");var subQ8=sQuery(id+"F0.wireOp",EDGE,"E1.top");var subQ9=sQuery(id+"F0.wireOp",EDGE,"E1.left");var subQ10=sQuery(id+"F0.wireOp",EDGE,"E23.filletArc");var subQ11=sQuery(id+"F0.wireOp",EDGE,"E24.filletArc");Q0=makeQuery(id+"F2.boolean.opBoolean","SPLIT",FACE,{"disambiguationData":[TD([makeQuery(id+"F1.opExtrude","SWEPT_FACE",FACE,{"disambiguationData":[OSD([subQ6])]})])],"derivedFrom":makeQuery(id+"F1.opExtrude","CAP_FACE",FACE,{"disambiguationData":[OSD([subQ6,subQ8,subQ9,subQ7,subQ4,subQ3,subQ2,subQ1,subQ0,subQ5,subQ10,subQ11])],"isStart":true})});}
            var sketch = newSketch(context, id + "F16", { "sketchPlane" : qUnion([Q0])});
            skLineSegment(sketch, "E79.0", {"start": v(-70, 90) * mm, "end": v(70, 90) * mm});
            skArc(sketch, "E80.0", {"start": v(-70, 90) * mm, "mid": v(-77.07, 87.07) * mm, "end": v(-80, 80) * mm});
            skLineSegment(sketch, "E81.0", {"start": v(-80, -80) * mm, "end": v(-80, 80) * mm});
            skArc(sketch, "E82.0", {"start": v(-80, -80) * mm, "mid": v(-77.07, -87.07) * mm, "end": v(-70, -90) * mm});
            skLineSegment(sketch, "E83.0", {"start": v(-70, -90) * mm, "end": v(70, -90) * mm});
            skArc(sketch, "E84.0", {"start": v(70, -90) * mm, "mid": v(77.07, -87.07) * mm, "end": v(80, -80) * mm});
            skLineSegment(sketch, "E85.0", {"start": v(80, -80) * mm, "end": v(80, 80) * mm});
            skArc(sketch, "E86.0", {"start": v(80, 80) * mm, "mid": v(77.07, 87.07) * mm, "end": v(70, 90) * mm});
            skCircle(sketch, "E87.0", {"center": v(60, 67.5) * mm, "radius": 4 * mm});
            skCircle(sketch, "E88.0", {"center": v(-60, 67.5) * mm, "radius": 4 * mm});
            skCircle(sketch, "E89.0", {"center": v(-60, -67.5) * mm, "radius": 4 * mm});
            skCircle(sketch, "E90.0", {"center": v(60, -67.5) * mm, "radius": 4 * mm});
            skArc(sketch, "E91.0", {"start": v(-56.15, -48.18) * mm, "mid": v(0, -67.5) * mm, "end": v(56.15, -48.18) * mm});
            skArc(sketch, "E92.0", {"start": v(56.15, -48.18) * mm, "mid": v(58.99, -44.68) * mm, "end": v(60, -40.3) * mm});
            skLineSegment(sketch, "E93.0", {"start": v(60, 40.3) * mm, "end": v(60, -40.3) * mm});
            skArc(sketch, "E94.0", {"start": v(56.15, 48.18) * mm, "mid": v(0, 67.5) * mm, "end": v(-56.15, 48.18) * mm});
            skArc(sketch, "E95.0", {"start": v(60, 40.3) * mm, "mid": v(58.99, 44.68) * mm, "end": v(56.15, 48.18) * mm});
            skArc(sketch, "E96.0", {"start": v(-56.15, 48.18) * mm, "mid": v(-58.99, 44.68) * mm, "end": v(-60, 40.3) * mm});
            skLineSegment(sketch, "E97.0", {"start": v(-60, 40.3) * mm, "end": v(-60, -40.3) * mm});
            skLineSegment(sketch, "E98.0.0", {"start": v(60, -40.3) * mm, "end": v(60, 40.3) * mm});
            skArc(sketch, "E98.0.5", {"start": v(-60, -40.3) * mm, "mid": v(-58.99, -44.68) * mm, "end": v(-56.15, -48.18) * mm});
            skLineSegment(sketch, "E99", {"start": v(0, 90) * mm, "end": v(0, 120) * mm, "construction": true});
            skCircle(sketch, "E100", {"center": v(0, 120) * mm, "radius": 6 * mm});
            skLineSegment(sketch, "E101", {"start": v(-14.5, 120) * mm, "end": v(-14.5, 108) * mm});
            skLineSegment(sketch, "E102", {"start": v(-14.5, 108) * mm, "end": v(-32.5, 90) * mm});
            skLineSegment(sketch, "E103", {"start": v(15.5, 120) * mm, "end": v(15.5, 108) * mm});
            skLineSegment(sketch, "E104", {"start": v(15.5, 108) * mm, "end": v(33.5, 90) * mm});
            skArc(sketch, "E105", {"start": v(15.5, 120) * mm, "mid": v(0.5, 135) * mm, "end": v(-14.5, 120) * mm});
            skLineSegment(sketch, "E106", {"start": v(-80, 0) * mm, "end": v(80, 0) * mm, "construction": true});
            skLineSegment(sketch, "E107.MirrorCS", {"start": v(-15.2, -120) * mm, "end": v(-15.2, -108) * mm});
            skLineSegment(sketch, "E108.MirrorCS", {"start": v(-15.2, -108) * mm, "end": v(-33.2, -90) * mm});
            skLineSegment(sketch, "E109.MirrorCS", {"start": v(14.8, -120) * mm, "end": v(14.8, -108) * mm});
            skLineSegment(sketch, "E110.MirrorCS", {"start": v(0, -90) * mm, "end": v(0, -120) * mm, "construction": true});
            skArc(sketch, "E111.MirrorCS", {"start": v(14.8, -120) * mm, "mid": v(-0.2, -135) * mm, "end": v(-15.2, -120) * mm});
            skLineSegment(sketch, "E112.MirrorCS", {"start": v(14.8, -108) * mm, "end": v(32.8, -90) * mm});
            skCircle(sketch, "E113.MirrorC", {"center": v(0, -120) * mm, "radius": 6 * mm});
            skSolve(sketch);
        }
        {
            var Q0;
            Q0 = qSketchRegion(id + "F16", true);
            var Q1;
            Q1=makeQuery(id+"F2.opExtrude","CAP_FACE",FACE,{"disambiguationData":[OSD([sQuery(id+"F0.wireOp",EDGE,"E12"),sQuery(id+"F0.wireOp",EDGE,"E13"),sQuery(id+"F0.wireOp",EDGE,"E14"),sQuery(id+"F0.wireOp",EDGE,"E15"),sQuery(id+"F0.wireOp",EDGE,"E17.filletArc"),sQuery(id+"F0.wireOp",EDGE,"E18.filletArc"),sQuery(id+"F0.wireOp",EDGE,"E19.filletArc"),sQuery(id+"F0.wireOp",EDGE,"E20.filletArc"),sQuery(id+"F0.wireOp",EDGE,"E25.0"),sQuery(id+"F0.wireOp",EDGE,"E25.1"),sQuery(id+"F0.wireOp",EDGE,"E25.2"),sQuery(id+"F0.wireOp",EDGE,"E25.3"),sQuery(id+"F0.wireOp",EDGE,"E25.4"),sQuery(id+"F0.wireOp",EDGE,"E25.5"),sQuery(id+"F0.wireOp",EDGE,"E25.6"),sQuery(id+"F0.wireOp",EDGE,"E25.7")])],"isStart":false});
            extrude(context, id + "F17", {"entities" : qUnion([Q0]), "endBound" : BoundingType.UP_TO_SURFACE, "depth" : 25 * mm, "endBoundEntityFace" : qUnion([Q1]), "offsetDistance" : 25 * mm});
        }
    });
